# Revit family: AcousticWoodDoors_AMBICO_SingleFrame
name_source: partatom
category: Doors
units: mm (PartAtom-declared; Revit-internal decimal feet)

## family parameters
Always vertical = Yes
Classification Number = 23.30.10.11.11
Cut with Voids When Loaded = No
Host = Wall
Room Calculation Point = No
Shared = No

## types (1)
- 3' x 7'
    Analytic Construction = <None>
    Date Updated = 2024/03/21
    Define Thermal Properties by = Schematic Type
    Description = STC39 to 46 Details Single Frame
    Fire Rating = 45, 90, 180
    Frame Width = 0' - 2"
    Function = Interior
    Height = 7' - 0"
    Manufacturer = AMBICO
    Maximum Height = 8' - 0"
    Maximum Width = 4' - 8"
    Minimum Height = 5' - 0"
    Minimum Width = 2' - 6"
    Model = STC39 to 46
    Operation = Swing
    Panel Material = AMBICO - Wood
    Product Material = AMBICO - Wood
    Product Page URL = https://www.ambico.com
    Rough Height = 7' - 2"
    Rough Width = 3' - 4"
    Thickness = 0' - 1 3/4"
    URL = https://www.ambico.com
    Version = 2
    Wall Closure = By host
    Warranty = Five (5) years from date of supply, covering material and workmanship.
    Width = 3' - 0"
    ZHeight = 7' - 0"
    ZWidth = 3' - 0"
    z_Door Side Gap = 0' - 0 1/8"

## geometry (parser evidence)
native form markers: Sweep x3
no freeform markers — native parametric forms only
